# Revit family: 10980600
name_source: partatom
category: Specialty Equipment
units: mm (PartAtom-declared; Revit-internal decimal feet)

## family parameters
Always vertical = Yes
Cut with Voids When Loaded = No
Enable Cutting in Views = Yes
Maintain Annotation Orientation = No
OmniClass Number = 23.40.40.00
OmniClass Title = Food Service Equipment and Furnishings
Part Type = Normal
Room Calculation Point = No
Round Connector Dimension = Use Diameter
Shared = No
Work Plane-Based = No

## types (1)
- Standard
    3D-Driven = Yes
    Area = 21,27 m²
    Center of Gravity = X: -42,779 mm Y: -142,794 mm Z: 589,790 mm
    Default Elevation = 0 mm  [stored 0 ft]
    Density = 1925,69 kg/m³
    Description = RBDM-600
    Design State = 1
    Manufacturer = RUSTFRIEBERGH A/S
    Mass = 142,44 kg
    Material = Generic
    Model = 10980600
    Part Number = 10980600_Simplify_1
    Requested Accuracy = Low
    URL = https://www.rustfriebergh.no
    Volume = 0,07 m³

note: [stored X ft] marks values corroborated as IEEE doubles in the binary element streams (Revit-internal decimal feet)

## geometry (parser evidence)
native form markers: Sweep x3
no freeform markers — native parametric forms only
